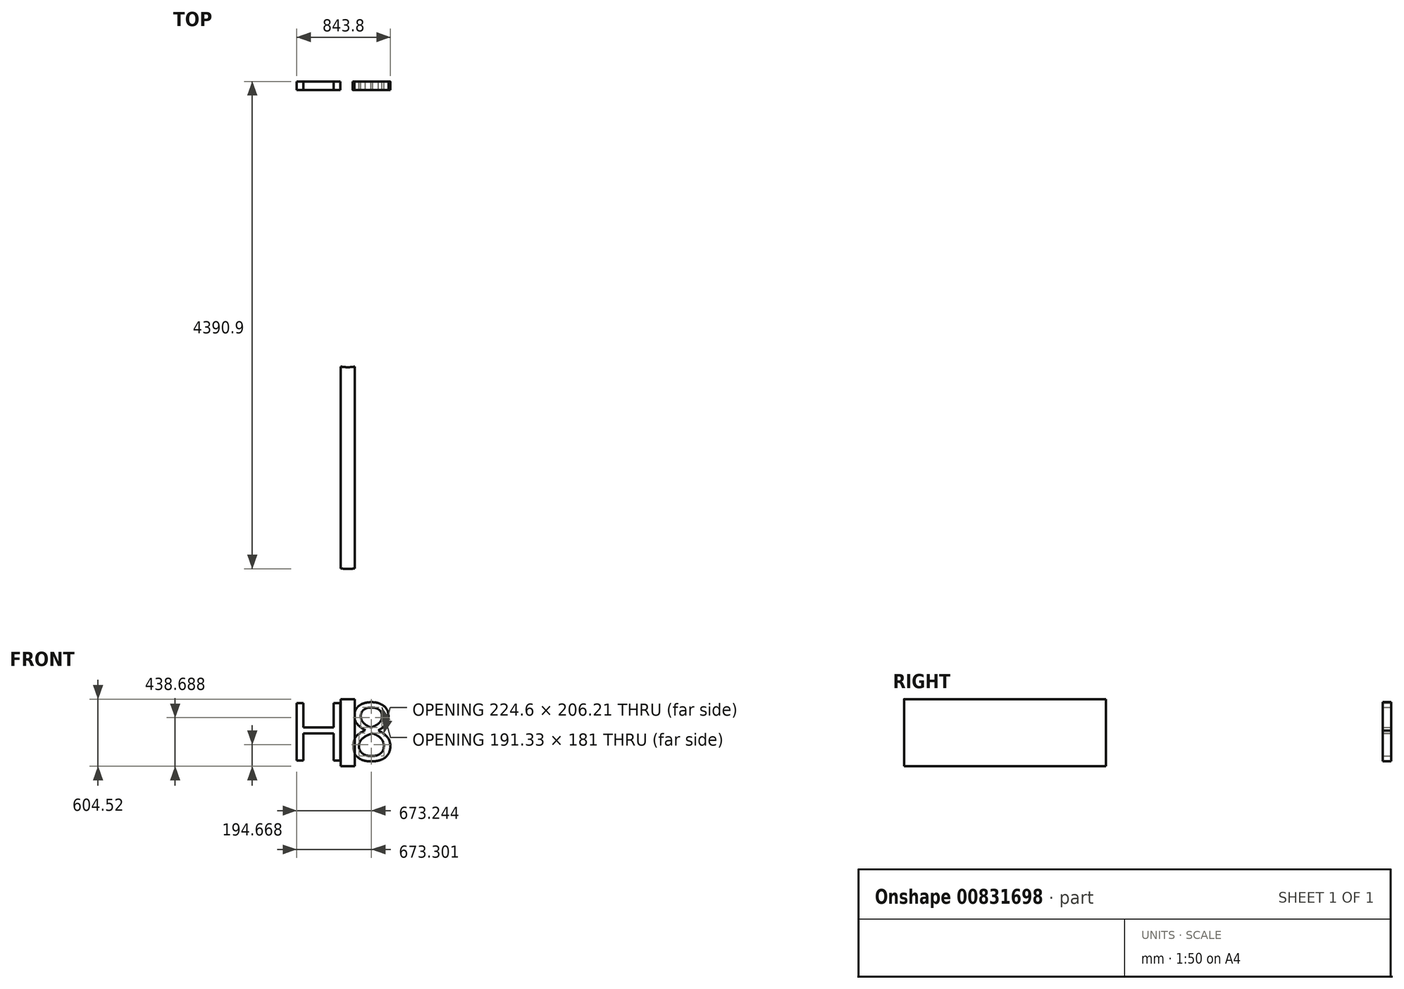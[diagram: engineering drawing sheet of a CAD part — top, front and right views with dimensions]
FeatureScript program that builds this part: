
annotation { "Feature Type Name" : "Feature", "Feature Type Description" : "" }
export const myFeature = defineFeature(function(context is Context, id is Id, definition is map)
    precondition{}
    {
        {
            var Q0;
            Q0=qCreatedBy(makeId("Top.planeOp"),FACE);
            var sketch = newSketch(context, id + "F0", { "sketchPlane" : qUnion([Q0])});
            skCircle(sketch, "E0", {"center": v(0, 0) * mm, "radius": 2120.9 * mm});
            skCircle(sketch, "E1", {"center": v(0, 0) * mm, "radius": 2184.4 * mm});
            skLineSegment(sketch, "E2", {"start": v(0, -2120.9) * mm, "end": v(0, 2120.9) * mm});
            skLineSegment(sketch, "E3", {"start": v(-2120.9, 0) * mm, "end": v(2120.9, 0) * mm});
            skLineSegment(sketch, "E4.0", {"start": v(63.5, -2209.8) * mm, "end": v(63.5, 2209.8) * mm});
            skLineSegment(sketch, "E5.0", {"start": v(-63.5, -2209.8) * mm, "end": v(-63.5, 2209.8) * mm});
            skLineSegment(sketch, "E6.0", {"start": v(-2209.8, -63.5) * mm, "end": v(2209.8, -63.5) * mm});
            skLineSegment(sketch, "E7.0", {"start": v(-2209.8, 63.5) * mm, "end": v(2209.8, 63.5) * mm});
            skLineSegment(sketch, "E8", {"start": v(0, 0) * mm, "end": v(-1544.6, 1544.6) * mm});
            skPoint(sketch, "E9", {"position": v(-63.5, 63.5) * mm});
            skPoint(sketch, "E10", {"position": v(-63.5, -63.5) * mm});
            skPoint(sketch, "E11", {"position": v(63.5, -63.5) * mm});
            skPoint(sketch, "E12", {"position": v(63.5, 63.5) * mm});
            skLineSegment(sketch, "E13", {"start": v(0, 0) * mm, "end": v(1544.6, 1544.6) * mm});
            skLineSegment(sketch, "E14", {"start": v(0, 0) * mm, "end": v(1544.6, -1544.6) * mm});
            skLineSegment(sketch, "E15", {"start": v(1544.6, -1544.6) * mm, "end": v(0, 0) * mm});
            skLineSegment(sketch, "E16", {"start": v(0, 0) * mm, "end": v(-1544.6, -1544.6) * mm});
            skCircle(sketch, "E17", {"center": v(0, 0) * mm, "radius": 368.3 * mm});
            skLineSegment(sketch, "E18", {"start": v(76.12, 368.3) * mm, "end": v(-63.5, 368.3) * mm});
            skLineSegment(sketch, "E19.0", {"start": v(25.58, 10.34) * mm, "end": v(-1519.02, 1554.94) * mm});
            skLineSegment(sketch, "E20.0", {"start": v(-10.34, -25.58) * mm, "end": v(-1554.94, 1519.02) * mm});
            skLineSegment(sketch, "E21.0", {"start": v(1570.18, -1534.26) * mm, "end": v(25.58, 10.34) * mm});
            skLineSegment(sketch, "E22.0", {"start": v(1534.26, -1570.18) * mm, "end": v(-10.34, -25.58) * mm});
            skLineSegment(sketch, "E23.0", {"start": v(-17.96, 17.96) * mm, "end": v(-1562.56, -1526.64) * mm});
            skLineSegment(sketch, "E24.0", {"start": v(17.96, -17.96) * mm, "end": v(-1526.64, -1562.56) * mm});
            skLineSegment(sketch, "E25.0", {"start": v(17.96, -17.96) * mm, "end": v(1562.56, 1526.64) * mm});
            skLineSegment(sketch, "E26.0", {"start": v(-17.96, 17.96) * mm, "end": v(1526.64, 1562.56) * mm});
            skSolve(sketch);
        }
        {
            var Q0;
            {var subQ0=sQuery(id+"F0.wireOp",EDGE,"E0");var subQ9=makeQuery(id+"F0.imprint","INTERSECT",VERTEX,{"disambiguationData":[OD(0.0)],"derivedFrom":[subQ0,sQuery(id+"F0.wireOp",EDGE,"E4.0")]});Q0=makeQuery(id+"F0.imprint","IMPRINT",FACE,{"disambiguationData":[TD([[makeQuery(id+"F0.imprint","IMPRINT",EDGE,{"disambiguationData":[TD([[subQ9,1.0]])],"derivedFrom":subQ0}),-1.0]])]});}
            var Q1;
            {var subQ0=sQuery(id+"F0.wireOp",EDGE,"E2");var subQ1=sQuery(id+"F0.wireOp",EDGE,"E0");var subQ2=makeQuery(id+"F0.imprint","INTERSECT",VERTEX,{"disambiguationData":[OD(1.0)],"derivedFrom":[subQ1,subQ0]});Q1=makeQuery(id+"F0.imprint","IMPRINT",FACE,{"disambiguationData":[TD([[makeQuery(id+"F0.imprint","IMPRINT",EDGE,{"disambiguationData":[TD([[subQ2,-1.0]])],"derivedFrom":subQ1}),1.0]])]});}
            var Q2;
            {var subQ3=sQuery(id+"F0.wireOp",EDGE,"E0");var subQ5=makeQuery(id+"F0.imprint","INTERSECT",VERTEX,{"disambiguationData":[OD(1.0)],"derivedFrom":[subQ3,sQuery(id+"F0.wireOp",EDGE,"E2")]});Q2=makeQuery(id+"F0.imprint","IMPRINT",FACE,{"disambiguationData":[TD([[makeQuery(id+"F0.imprint","IMPRINT",EDGE,{"disambiguationData":[TD([[subQ5,1.0]])],"derivedFrom":subQ3}),-1.0]])]});}
            var Q3;
            {var subQ0=sQuery(id+"F0.wireOp",EDGE,"E5.0");var subQ1=sQuery(id+"F0.wireOp",EDGE,"E0");var subQ2=makeQuery(id+"F0.imprint","INTERSECT",VERTEX,{"disambiguationData":[OD(0.0)],"derivedFrom":[subQ1,subQ0]});Q3=makeQuery(id+"F0.imprint","IMPRINT",FACE,{"disambiguationData":[TD([[makeQuery(id+"F0.imprint","IMPRINT",EDGE,{"disambiguationData":[TD([[subQ2,-1.0]])],"derivedFrom":subQ1}),-1.0]])]});}
            var Q4;
            {var subQ0=sQuery(id+"F0.wireOp",EDGE,"E2");var subQ1=sQuery(id+"F0.wireOp",EDGE,"E0");var subQ2=makeQuery(id+"F0.imprint","INTERSECT",VERTEX,{"disambiguationData":[OD(1.0)],"derivedFrom":[subQ1,subQ0]});Q4=makeQuery(id+"F0.imprint","IMPRINT",FACE,{"disambiguationData":[TD([[makeQuery(id+"F0.imprint","IMPRINT",EDGE,{"disambiguationData":[TD([[subQ2,1.0]])],"derivedFrom":subQ1}),1.0]])]});}
            extrude(context, id + "F1", {"entities" : qUnion([Q0, Q1, Q2, Q3, Q4]), "depth" : 604.52 * mm, "offsetDistance" : 25.4 * mm});
        }
        {
            var Q0;
            Q0=makeQuery(id+"F1.opExtrude","CAP_FACE",FACE,{"disambiguationData":[OSD([sQuery(id+"F0.wireOp",EDGE,"E0"),sQuery(id+"F0.wireOp",EDGE,"E1"),sQuery(id+"F0.wireOp",EDGE,"E4.0"),sQuery(id+"F0.wireOp",EDGE,"E5.0"),sQuery(id+"F0.wireOp",EDGE,"E7.0"),sQuery(id+"F0.wireOp",EDGE,"E8"),sQuery(id+"F0.wireOp",EDGE,"E13")])],"isStart":false});
            var sketch = newSketch(context, id + "F2", { "sketchPlane" : qUnion([Q0])});
            skCircle(sketch, "E27", {"center": v(0, 447.04) * mm, "radius": 35.56 * mm});
            skSolve(sketch);
        }
        {
            var Q0;
            Q0=makeQuery(id+"F2.imprint","IMPRINT",FACE,{"disambiguationData":[TD([[makeQuery(id+"F2.imprint","IMPRINT",EDGE,{"derivedFrom":sQuery(id+"F2.wireOp",EDGE,"E27")}),1.0]])]});
            extrude(context, id + "F3", {"entities" : qUnion([Q0]), "operationType" : NewBodyOperationType.REMOVE, "oppositeDirection" : true, "depth" : 660.4 * mm, "offsetDistance" : 25.4 * mm});
        }
        {
            var Q0;
            Q0=qCreatedBy(makeId("Front.planeOp"),FACE);
            cPlane(context, id + "F4", {"entities" : qUnion([Q0]), "cplaneType" : CPlaneType.OFFSET, "offset" : 2209.8 * mm, "oppositeDirection" : true, "width" : 152.4 * mm, "height" : 152.4 * mm});
        }
        {
            var Q0;
            Q0=qCreatedBy(id+"F4.planeOp",FACE);
            var sketch = newSketch(context, id + "F5", { "sketchPlane" : qUnion([Q0])});
            skText(sketch, "E28", { "text": "8H", "fontName": "OpenSans-Regular.ttf"});
            const initialGuessF5  = {"E28": [-0.4639, 0.0508, 1, 0, 0.52324]};
            skSetInitialGuess(sketch, initialGuessF5);
            skSolve(sketch);
        }
        {
            var Q0;
            Q0 = qSketchRegion(id + "F5", true);
            extrude(context, id + "F6", {"entities" : qUnion([Q0]), "oppositeDirection" : true, "depth" : 76.2 * mm, "offsetDistance" : 25.4 * mm});
        }
        {
            var Q0;
            Q0=makeQuery(id+"F6.opExtrude","SWEPT_BODY",BODY,{"disambiguationData":[OSD([sQuery(id+"F5.wireOp",EDGE,"E28.sketch_text.stroke-31"),sQuery(id+"F5.wireOp",EDGE,"E28.sketch_text.stroke-32"),sQuery(id+"F5.wireOp",EDGE,"E28.sketch_text.stroke-33"),sQuery(id+"F5.wireOp",EDGE,"E28.sketch_text.stroke-34"),sQuery(id+"F5.wireOp",EDGE,"E28.sketch_text.stroke-35"),sQuery(id+"F5.wireOp",EDGE,"E28.sketch_text.stroke-36"),sQuery(id+"F5.wireOp",EDGE,"E28.sketch_text.stroke-37"),sQuery(id+"F5.wireOp",EDGE,"E28.sketch_text.stroke-38"),sQuery(id+"F5.wireOp",EDGE,"E28.sketch_text.stroke-39"),sQuery(id+"F5.wireOp",EDGE,"E28.sketch_text.stroke-40"),sQuery(id+"F5.wireOp",EDGE,"E28.sketch_text.stroke-41"),sQuery(id+"F5.wireOp",EDGE,"E28.sketch_text.stroke-42")])]});
            var Q1;
            Q1=makeQuery(id+"F6.opExtrude","SWEPT_BODY",BODY,{"disambiguationData":[OSD([sQuery(id+"F5.wireOp",EDGE,"E28.sketch_text.stroke-0"),sQuery(id+"F5.wireOp",EDGE,"E28.sketch_text.stroke-1"),sQuery(id+"F5.wireOp",EDGE,"E28.sketch_text.stroke-2"),sQuery(id+"F5.wireOp",EDGE,"E28.sketch_text.stroke-3"),sQuery(id+"F5.wireOp",EDGE,"E28.sketch_text.stroke-4"),sQuery(id+"F5.wireOp",EDGE,"E28.sketch_text.stroke-5"),sQuery(id+"F5.wireOp",EDGE,"E28.sketch_text.stroke-6"),sQuery(id+"F5.wireOp",EDGE,"E28.sketch_text.stroke-7"),sQuery(id+"F5.wireOp",EDGE,"E28.sketch_text.stroke-8"),sQuery(id+"F5.wireOp",EDGE,"E28.sketch_text.stroke-9"),sQuery(id+"F5.wireOp",EDGE,"E28.sketch_text.stroke-10"),sQuery(id+"F5.wireOp",EDGE,"E28.sketch_text.stroke-11"),sQuery(id+"F5.wireOp",EDGE,"E28.sketch_text.stroke-12"),sQuery(id+"F5.wireOp",EDGE,"E28.sketch_text.stroke-13"),sQuery(id+"F5.wireOp",EDGE,"E28.sketch_text.stroke-14"),sQuery(id+"F5.wireOp",EDGE,"E28.sketch_text.stroke-15"),sQuery(id+"F5.wireOp",EDGE,"E28.sketch_text.stroke-16"),sQuery(id+"F5.wireOp",EDGE,"E28.sketch_text.stroke-17"),sQuery(id+"F5.wireOp",EDGE,"E28.sketch_text.stroke-18"),sQuery(id+"F5.wireOp",EDGE,"E28.sketch_text.stroke-19"),sQuery(id+"F5.wireOp",EDGE,"E28.sketch_text.stroke-20"),sQuery(id+"F5.wireOp",EDGE,"E28.sketch_text.stroke-21"),sQuery(id+"F5.wireOp",EDGE,"E28.sketch_text.stroke-22"),sQuery(id+"F5.wireOp",EDGE,"E28.sketch_text.stroke-23"),sQuery(id+"F5.wireOp",EDGE,"E28.sketch_text.stroke-24"),sQuery(id+"F5.wireOp",EDGE,"E28.sketch_text.stroke-25"),sQuery(id+"F5.wireOp",EDGE,"E28.sketch_text.stroke-26"),sQuery(id+"F5.wireOp",EDGE,"E28.sketch_text.stroke-27"),sQuery(id+"F5.wireOp",EDGE,"E28.sketch_text.stroke-28"),sQuery(id+"F5.wireOp",EDGE,"E28.sketch_text.stroke-29"),sQuery(id+"F5.wireOp",EDGE,"E28.sketch_text.stroke-30")])]});
            var Q2;
            Q2=makeQuery(id+"F6.opExtrude","CAP_EDGE",EDGE,{"disambiguationData":[OSD([sQuery(id+"F5.wireOp",EDGE,"E28.sketch_text.stroke-36")])],"isStart":false});
            transform(context, id + "F7", {"entities" : qUnion([Q0, Q1]), "transformType" : TransformType.ROTATION, "transformAxis" : qUnion([Q2]), "angle" : 180 * degree, "makeCopy" : false});
        }
        {
            var Q0;
            Q0=makeQuery(id+"F6.opExtrude","SWEPT_BODY",BODY,{"disambiguationData":[OSD([sQuery(id+"F5.wireOp",EDGE,"E28.sketch_text.stroke-0"),sQuery(id+"F5.wireOp",EDGE,"E28.sketch_text.stroke-1"),sQuery(id+"F5.wireOp",EDGE,"E28.sketch_text.stroke-2"),sQuery(id+"F5.wireOp",EDGE,"E28.sketch_text.stroke-3"),sQuery(id+"F5.wireOp",EDGE,"E28.sketch_text.stroke-4"),sQuery(id+"F5.wireOp",EDGE,"E28.sketch_text.stroke-5"),sQuery(id+"F5.wireOp",EDGE,"E28.sketch_text.stroke-6"),sQuery(id+"F5.wireOp",EDGE,"E28.sketch_text.stroke-7"),sQuery(id+"F5.wireOp",EDGE,"E28.sketch_text.stroke-8"),sQuery(id+"F5.wireOp",EDGE,"E28.sketch_text.stroke-9"),sQuery(id+"F5.wireOp",EDGE,"E28.sketch_text.stroke-10"),sQuery(id+"F5.wireOp",EDGE,"E28.sketch_text.stroke-11"),sQuery(id+"F5.wireOp",EDGE,"E28.sketch_text.stroke-12"),sQuery(id+"F5.wireOp",EDGE,"E28.sketch_text.stroke-13"),sQuery(id+"F5.wireOp",EDGE,"E28.sketch_text.stroke-14"),sQuery(id+"F5.wireOp",EDGE,"E28.sketch_text.stroke-15"),sQuery(id+"F5.wireOp",EDGE,"E28.sketch_text.stroke-16"),sQuery(id+"F5.wireOp",EDGE,"E28.sketch_text.stroke-17"),sQuery(id+"F5.wireOp",EDGE,"E28.sketch_text.stroke-18"),sQuery(id+"F5.wireOp",EDGE,"E28.sketch_text.stroke-19"),sQuery(id+"F5.wireOp",EDGE,"E28.sketch_text.stroke-20"),sQuery(id+"F5.wireOp",EDGE,"E28.sketch_text.stroke-21"),sQuery(id+"F5.wireOp",EDGE,"E28.sketch_text.stroke-22"),sQuery(id+"F5.wireOp",EDGE,"E28.sketch_text.stroke-23"),sQuery(id+"F5.wireOp",EDGE,"E28.sketch_text.stroke-24"),sQuery(id+"F5.wireOp",EDGE,"E28.sketch_text.stroke-25"),sQuery(id+"F5.wireOp",EDGE,"E28.sketch_text.stroke-26"),sQuery(id+"F5.wireOp",EDGE,"E28.sketch_text.stroke-27"),sQuery(id+"F5.wireOp",EDGE,"E28.sketch_text.stroke-28"),sQuery(id+"F5.wireOp",EDGE,"E28.sketch_text.stroke-29"),sQuery(id+"F5.wireOp",EDGE,"E28.sketch_text.stroke-30")])]});
            var Q1;
            Q1=makeQuery(id+"F6.opExtrude","SWEPT_BODY",BODY,{"disambiguationData":[OSD([sQuery(id+"F5.wireOp",EDGE,"E28.sketch_text.stroke-31"),sQuery(id+"F5.wireOp",EDGE,"E28.sketch_text.stroke-32"),sQuery(id+"F5.wireOp",EDGE,"E28.sketch_text.stroke-33"),sQuery(id+"F5.wireOp",EDGE,"E28.sketch_text.stroke-34"),sQuery(id+"F5.wireOp",EDGE,"E28.sketch_text.stroke-35"),sQuery(id+"F5.wireOp",EDGE,"E28.sketch_text.stroke-36"),sQuery(id+"F5.wireOp",EDGE,"E28.sketch_text.stroke-37"),sQuery(id+"F5.wireOp",EDGE,"E28.sketch_text.stroke-38"),sQuery(id+"F5.wireOp",EDGE,"E28.sketch_text.stroke-39"),sQuery(id+"F5.wireOp",EDGE,"E28.sketch_text.stroke-40"),sQuery(id+"F5.wireOp",EDGE,"E28.sketch_text.stroke-41"),sQuery(id+"F5.wireOp",EDGE,"E28.sketch_text.stroke-42")])]});
            transform(context, id + "F8", {"entities" : qUnion([Q0, Q1]), "transformType" : TransformType.TRANSLATION_3D, "dx" : -90.17 * mm, "dy" : -155.7 * mm, "dz" : 0 * mm, "makeCopy" : false});
        }
    });
